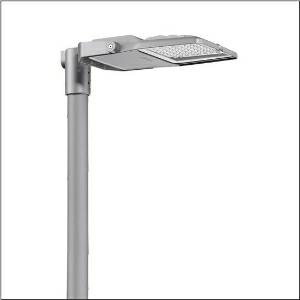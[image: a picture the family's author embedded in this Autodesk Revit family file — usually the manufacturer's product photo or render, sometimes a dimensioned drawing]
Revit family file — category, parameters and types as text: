
# Revit family: floodlight_fl_21_iq_mini___pl52_5xa7771b2d3a_cd8f
name_source: partatom
category: Lighting Fixtures
units: mm (PartAtom-declared; Revit-internal decimal feet)

## family parameters
Cut with Voids When Loaded = No
Host = Face
Light Source = No
Part Type = Normal
Room Calculation Point = No
Round Connector Dimension = Use Diameter
Shared = No

## types (1)
- --- (1 x LED, 6240 lm, 45.5 W, 3000K)
    Apparent Load = 46 VA
    CIE Flux Codes = 26 60 98 100 100
    Color Rendering = 70
    Color Temperature = 3000K
    Default Elevation = 1800 mm
    Description = Floodlight FL 21 iQ mini, floodlight, primary light control with lens, of PMMA, primary optical cover: protective disc, of toughened safety glass, transparent, light distribution: PL52, light emission: direct distribution, installation type: surface-mounted, LED, High Power LED, rated luminous flux: 6.240lm, luminous efficacy: 137lm/W, light colour: 730, colour temperature: 3000K, control gear: iQ Comfort/DALI, control: Auto-Match, Temp-Guard, Lumen-Switch, Night-Set, Smart-Wire, Light-Fading, Desk-Remote (wireless, voltage-free reading and setting of iQ features in the workshop via application-optimized NFC function/RFID function), optimised constant luminous flux control (CLO 2.0), with terminal, 6-pole, mains connection: 220..240V, AC, 50/60Hz, start of lifetime: 46W, end of service life: 48W, reduction: 22W, luminaire housing, of diecast aluminium, powder-coated, Siteco® metallic grey (DB 702S), corrosivity category C5 mid according to DIN EN ISO 12944, suitable for swimming pools, chlorine-resistant, sealing non-destructively replaceable, please order mast flange separately, mast bracket, of steel, galvanised, powder-coated, Siteco® metallic grey (DB 702S), protection rating (complete): IP66, insulation class (complete): insulation class II (safety insulation), certification: CE, ENEC, VDE, protection symbol: D, impact resistance: IK08, permissible operating ambient temperature: -40..+40°C, permissible operating ambient temperature for outdoor applications: -40..+50°C, standard: DIN EN 12944, LABS conformity tested according to VDMA 24364:2018-05, packaging unit: 1 piece

Light Distribution: PL52
    Height = 70 mm
    Lamp = 1 x LED
    Lamp Light Flux = 6240 lm
    Lamp Power = 45.5 W
    Lamp count = 1
    Length = 485 mm
    Luminous efficacy = 137 lm/W
    Manufacturer = Siteco
    ModVariant = No
    Model = 5XA7771B2D3A
    Number of Poles = 1
    OnlyDefault = Yes
    Power Factor = 1
    Product Name = Floodlight FL 21 iQ mini | PL52
    Product group = floodlight | pylon annexe
    ProductGroupID = 6200
    Protection Class = Protection class II
    Protection Degree = IP 66
    RLX_Detail_Level = 1
    RLX_Emergency_Light_Flux = 0 lm
    RLX_Emergency_Type = 0
    RLX_Emergency_Type_DB = No
    RlxData = <blob elided: 101357 chars, md5=2cad9dae>
    Socket = socket
    Standby Power = 0 W
    System Light Flux = 6240 lm
    System Power = 46 W
    Type Comments = factory setting: luminous flux: 100 % | dim-lin: 254 | 463 mA
    Type Image = l_1007125.jpg
    URL = http://relux.com
    VarID = @adj_165096
    Voltage = 0 V
    Weight = 0.00 kg
    Width = 337 mm

## geometry (parser evidence)
native form markers: Blend x4, Sweep x13
no freeform markers — native parametric forms only
